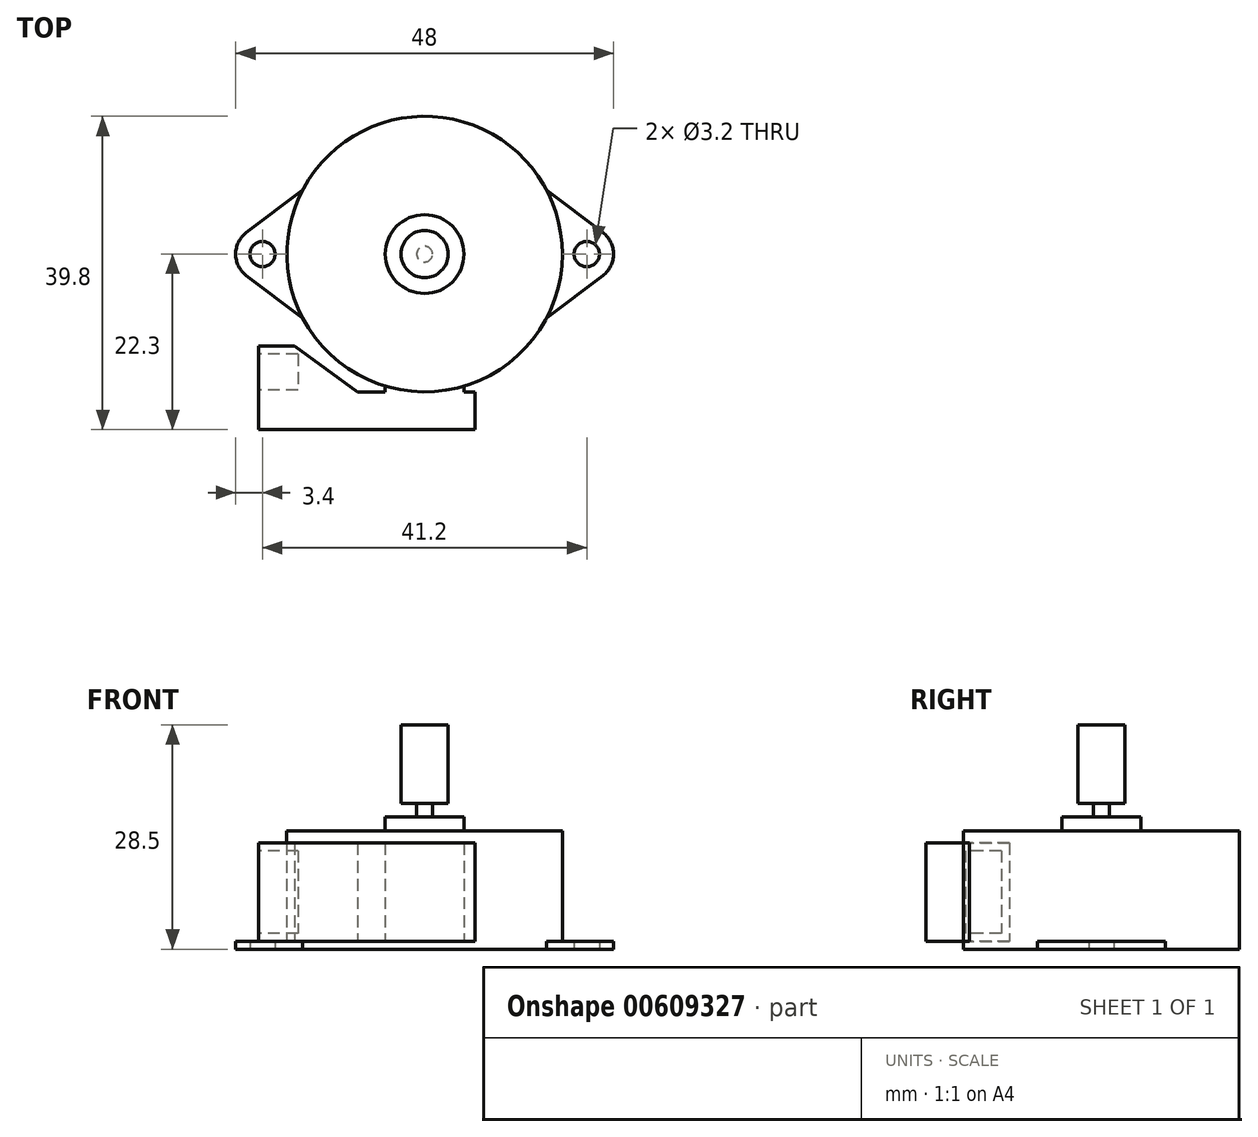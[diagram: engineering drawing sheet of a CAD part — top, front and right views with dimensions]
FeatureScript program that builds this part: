
annotation { "Feature Type Name" : "Feature", "Feature Type Description" : "" }
export const myFeature = defineFeature(function(context is Context, id is Id, definition is map)
    precondition{}
    {
        {
            var Q0;
            Q0=qCreatedBy(makeId("Top.planeOp"),FACE);
            var sketch = newSketch(context, id + "F0", { "sketchPlane" : qUnion([Q0])});
            skCircle(sketch, "E0", {"center": v(0, 0) * mm, "radius": 17.5 * mm});
            skCircle(sketch, "E1", {"center": v(-20.6, 0) * mm, "radius": 1.6 * mm});
            skCircle(sketch, "E2", {"center": v(-20.6, 0) * mm, "radius": 3.4 * mm});
            skLineSegment(sketch, "E3", {"start": v(-22.65, 2.71) * mm, "end": v(-15.5, 8.12) * mm});
            skLineSegment(sketch, "E4", {"start": v(-15.5, 8.12) * mm, "end": v(-15.5, -8.12) * mm});
            skLineSegment(sketch, "E5", {"start": v(-15.5, -8.12) * mm, "end": v(-22.65, -2.71) * mm});
            skLineSegment(sketch, "E6", {"start": v(-22.65, -2.71) * mm, "end": v(-22.65, 2.71) * mm});
            skLineSegment(sketch, "E7.MirrorCS", {"start": v(15.5, 8.12) * mm, "end": v(15.5, -8.12) * mm});
            skLineSegment(sketch, "E8.MirrorCS", {"start": v(15.5, -8.12) * mm, "end": v(22.65, -2.71) * mm});
            skLineSegment(sketch, "E9.MirrorCS", {"start": v(22.65, 2.71) * mm, "end": v(15.5, 8.12) * mm});
            skCircle(sketch, "E10.MirrorC", {"center": v(20.6, 0) * mm, "radius": 3.4 * mm});
            skCircle(sketch, "E11.MirrorC", {"center": v(20.6, 0) * mm, "radius": 1.6 * mm});
            skLineSegment(sketch, "E12.MirrorCS", {"start": v(22.65, -2.71) * mm, "end": v(22.65, 2.71) * mm});
            skSolve(sketch);
        }
        {
            var Q0;
            Q0 = qSketchRegion(id + "F0", true);
            var Q1;
            {var subQ0=sQuery(id+"F0.wireOp",EDGE,"E2");var subQ1=sQuery(id+"F0.wireOp",EDGE,"E0");var subQ2=makeQuery(id+"F0.imprint","INTERSECT",VERTEX,{"disambiguationData":[OD(0.0)],"derivedFrom":[subQ1,subQ0]});Q1=makeQuery(id+"F0.imprint","IMPRINT",FACE,{"disambiguationData":[TD([[makeQuery(id+"F0.imprint","IMPRINT",EDGE,{"disambiguationData":[TD([[subQ2,-1.0]])],"derivedFrom":subQ1}),1.0]])]});}
            var Q2;
            {var subQ0=sQuery(id+"F0.wireOp",EDGE,"E10.MirrorC");var subQ1=sQuery(id+"F0.wireOp",EDGE,"E0");var subQ2=makeQuery(id+"F0.imprint","INTERSECT",VERTEX,{"disambiguationData":[OD(0.0)],"derivedFrom":[subQ1,subQ0]});Q2=makeQuery(id+"F0.imprint","IMPRINT",FACE,{"disambiguationData":[TD([[makeQuery(id+"F0.imprint","IMPRINT",EDGE,{"disambiguationData":[TD([[subQ2,1.0]])],"derivedFrom":subQ1}),1.0]])]});}
            extrude(context, id + "F1", {"entities" : qUnion([Q0, Q1, Q2]), "depth" : 1 * mm, "offsetDistance" : 25.4 * mm});
        }
        {
            var Q0;
            Q0=makeQuery(id+"F1.opExtrude","CAP_FACE",FACE,{"disambiguationData":[OSD([sQuery(id+"F0.wireOp",EDGE,"E0"),sQuery(id+"F0.wireOp",EDGE,"E1"),sQuery(id+"F0.wireOp",EDGE,"E2"),sQuery(id+"F0.wireOp",EDGE,"E3"),sQuery(id+"F0.wireOp",EDGE,"E5"),sQuery(id+"F0.wireOp",EDGE,"E8.MirrorCS"),sQuery(id+"F0.wireOp",EDGE,"E9.MirrorCS"),sQuery(id+"F0.wireOp",EDGE,"E10.MirrorC"),sQuery(id+"F0.wireOp",EDGE,"E11.MirrorC")])],"isStart":false});
            var sketch = newSketch(context, id + "F2", { "sketchPlane" : qUnion([Q0])});
            skCircle(sketch, "E13", {"center": v(0, 0) * mm, "radius": 17.5 * mm});
            skLineSegment(sketch, "E14.bottom", {"start": v(-21.1, -17.5) * mm, "end": v(6.4, -17.5) * mm});
            skLineSegment(sketch, "E14.top", {"start": v(-21.1, -22.3) * mm, "end": v(6.4, -22.3) * mm});
            skLineSegment(sketch, "E14.left", {"start": v(-21.1, -17.5) * mm, "end": v(-21.1, -22.3) * mm});
            skLineSegment(sketch, "E14.right", {"start": v(6.4, -17.5) * mm, "end": v(6.4, -22.3) * mm});
            skLineSegment(sketch, "E15", {"start": v(-21.1, -17.5) * mm, "end": v(-21.1, -11.7) * mm});
            skLineSegment(sketch, "E16", {"start": v(-21.1, -11.7) * mm, "end": v(-16.5, -11.7) * mm});
            skLineSegment(sketch, "E17", {"start": v(-16.5, -11.7) * mm, "end": v(-8.48, -17.5) * mm});
            skLineSegment(sketch, "E18.bottom", {"start": v(-5, 0) * mm, "end": v(5, 0) * mm});
            skLineSegment(sketch, "E18.top", {"start": v(-5, -22.3) * mm, "end": v(5, -22.3) * mm});
            skLineSegment(sketch, "E18.left", {"start": v(-5, 0) * mm, "end": v(-5, -22.3) * mm});
            skLineSegment(sketch, "E18.right", {"start": v(5, 0) * mm, "end": v(5, -22.3) * mm});
            skSolve(sketch);
        }
        {
            var Q0;
            {var subQ5=sQuery(id+"F2.wireOp",EDGE,"E18.bottom");Q0=makeQuery(id+"F2.imprint","IMPRINT",FACE,{"disambiguationData":[TD([[makeQuery(id+"F2.imprint","IMPRINT",EDGE,{"derivedFrom":subQ5}),1.0]])]});}
            var Q1;
            {var subQ1=sQuery(id+"F2.wireOp",EDGE,"E18.bottom");Q1=makeQuery(id+"F2.imprint","IMPRINT",FACE,{"disambiguationData":[TD([[makeQuery(id+"F2.imprint","IMPRINT",EDGE,{"derivedFrom":subQ1}),-1.0]])]});}
            extrude(context, id + "F3", {"entities" : qUnion([Q0, Q1]), "operationType" : NewBodyOperationType.ADD, "depth" : 14 * mm, "offsetDistance" : 25.4 * mm});
        }
        {
            var Q0;
            Q0 = qSketchRegion(id + "F2", true);
            extrude(context, id + "F4", {"entities" : qUnion([Q0]), "operationType" : NewBodyOperationType.ADD, "depth" : 12.5 * mm, "offsetDistance" : 25.4 * mm});
        }
        {
            var Q0;
            Q0=makeQuery(id+"F3.opExtrude","CAP_FACE",FACE,{"disambiguationData":[OSD([sQuery(id+"F2.wireOp",EDGE,"E13")])],"isStart":false});
            var sketch = newSketch(context, id + "F5", { "sketchPlane" : qUnion([Q0])});
            skCircle(sketch, "E19", {"center": v(0, 0) * mm, "radius": 5 * mm});
            skSolve(sketch);
        }
        {
            var Q0;
            Q0 = qSketchRegion(id + "F5", true);
            extrude(context, id + "F6", {"entities" : qUnion([Q0]), "operationType" : NewBodyOperationType.ADD, "depth" : 1.8 * mm, "offsetDistance" : 25.4 * mm});
        }
        {
            var Q0;
            Q0=makeQuery(id+"F6.opExtrude","CAP_FACE",FACE,{"disambiguationData":[OSD([sQuery(id+"F5.wireOp",EDGE,"E19")])],"isStart":false});
            var sketch = newSketch(context, id + "F7", { "sketchPlane" : qUnion([Q0])});
            skCircle(sketch, "E20", {"center": v(0, 0) * mm, "radius": 1 * mm});
            skSolve(sketch);
        }
        {
            var Q0;
            Q0 = qSketchRegion(id + "F7", true);
            extrude(context, id + "F8", {"entities" : qUnion([Q0]), "operationType" : NewBodyOperationType.ADD, "depth" : 1.7 * mm, "offsetDistance" : 25.4 * mm});
        }
        {
            var Q0;
            Q0=makeQuery(id+"F8.opExtrude","CAP_FACE",FACE,{"disambiguationData":[OSD([sQuery(id+"F7.wireOp",EDGE,"E20")])],"isStart":false});
            var sketch = newSketch(context, id + "F9", { "sketchPlane" : qUnion([Q0])});
            skCircle(sketch, "E21", {"center": v(0, 0) * mm, "radius": 3 * mm});
            skSolve(sketch);
        }
        {
            var Q0;
            Q0 = qSketchRegion(id + "F9", true);
            extrude(context, id + "F10", {"entities" : qUnion([Q0]), "operationType" : NewBodyOperationType.ADD, "depth" : 10 * mm, "offsetDistance" : 25.4 * mm});
        }
        {
            var Q0;
            Q0=makeQuery(id+"F4.opExtrude","SWEPT_FACE",FACE,{"disambiguationData":[OSD([sQuery(id+"F2.wireOp",EDGE,"E14.left"),sQuery(id+"F2.wireOp",EDGE,"E15")])]});
            var sketch = newSketch(context, id + "F11", { "sketchPlane" : qUnion([Q0])});
            skLineSegment(sketch, "E22.bottom", {"start": v(12.7, 12.5) * mm, "end": v(17.3, 12.5) * mm});
            skLineSegment(sketch, "E22.top", {"start": v(12.7, 2) * mm, "end": v(17.3, 2) * mm});
            skLineSegment(sketch, "E22.left", {"start": v(12.7, 12.5) * mm, "end": v(12.7, 2) * mm});
            skLineSegment(sketch, "E22.right", {"start": v(17.3, 12.5) * mm, "end": v(17.3, 2) * mm});
            skSolve(sketch);
        }
        {
            var Q0;
            Q0 = qSketchRegion(id + "F11", true);
            extrude(context, id + "F12", {"entities" : qUnion([Q0]), "operationType" : NewBodyOperationType.REMOVE, "oppositeDirection" : true, "depth" : 5 * mm, "offsetDistance" : 25.4 * mm});
        }
    });
